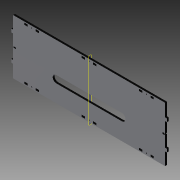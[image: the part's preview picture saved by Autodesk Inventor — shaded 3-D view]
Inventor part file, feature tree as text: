
AUTODESK INVENTOR PART (.ipt)
format: ipt  version: 2013 (Build 170138000, 138)  size: 269,312 bytes
history: native  units: in
note: dims shown in document units (in); Inventor stores cm internally (conversion verified against a paired STEP export)
features: reference x14, extrude x6, sketch x6, plane x1, mirror x1
ambient origin geometry x8: Origin, YZ Plane, XZ Plane, XY Plane, X Axis, Y Axis, Z Axis, Center Point
bodies: Solid1 (feature_tree)
feature tree (28):
  extrude  "Extrusion1"  Depth=0.1181in
  extrude  "Extrusion2"  Depth=0.225in TaperAngle=0.0deg
  extrude  "Extrusion3"  Depth=0.1181in
  extrude  "Extrusion4"  Depth=0.1181in
  plane  "Work Plane1"
  extrude  "Extrusion5"  Depth=0.1181in
  mirror  "Mirror1"
  extrude  "Extrusion6"  Depth=0.1181in
  sketch  "Sketch1"  dims[d0=0.1181in d1=0.1181in]
  sketch  "Sketch2"  dims[d2=0.225in d3=0.0in d4=0.225in d5=0.0in]
  reference  "Reference1"
  reference  "Reference2"
  reference  "Reference3"
  reference  "Reference4"
  reference  "Reference5"
  reference  "Reference6"
  reference  "Reference7"
  reference  "Reference8"
  reference  "Reference9"
  reference  "Reference10"
  reference  "Reference11"
  reference  "Reference12"
  sketch  "Sketch3"  dims[d6=0.1181in d8=0.1181in]
  sketch  "Sketch4"  dims[d9=0.1181in d10=0.1181in]
  sketch  "Sketch5"  dims[d11=0.1181in d12=0.1181in]
  sketch  "Sketch6"  dims[d13=0.225in d14=0.0in d15=0.1181in d17=0.2165in d18=0.2474in d19=0.0787in d20=0.3262in d21=0.225in d22=0.0in d23=1.378in d26=0.225in d27=0.3937in d28=0.225in d29=0.0in d30=7.874in d32=0.8661in d33=1.0in d34=0.0in]
  reference  "Reference13"
  reference  "Reference14"
